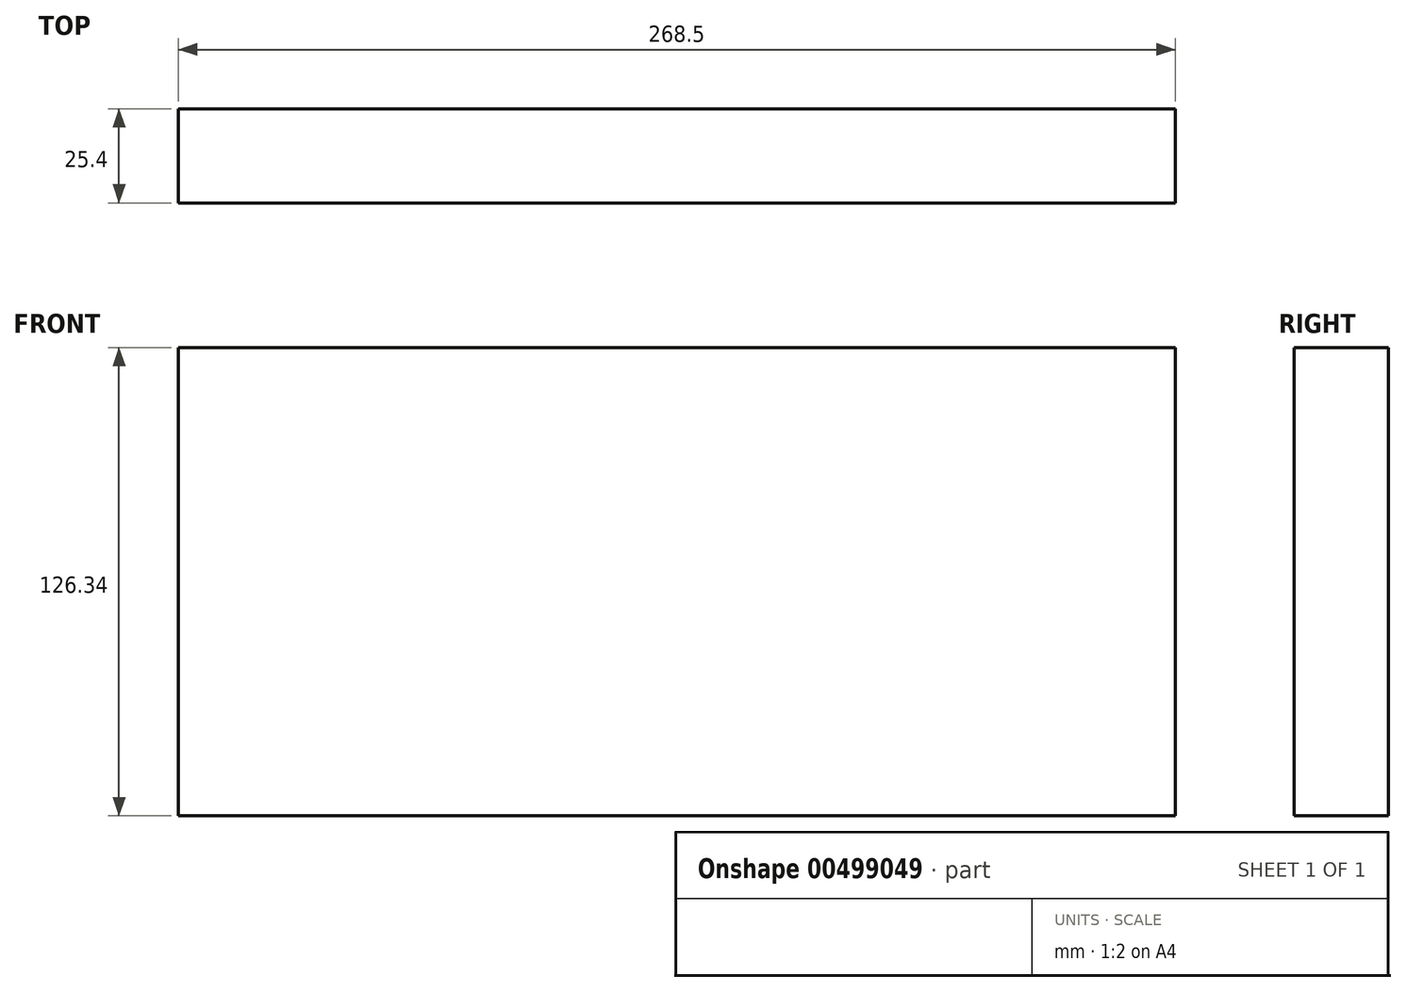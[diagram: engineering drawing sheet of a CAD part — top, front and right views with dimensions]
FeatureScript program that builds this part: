
annotation { "Feature Type Name" : "Feature", "Feature Type Description" : "" }
export const myFeature = defineFeature(function(context is Context, id is Id, definition is map)
    precondition{}
    {
        {
            var Q0;
            Q0=qCreatedBy(makeId("Front.planeOp"),FACE);
            var sketch = newSketch(context, id + "F0", { "sketchPlane" : qUnion([Q0])});
            skLineSegment(sketch, "E0.bottom", {"start": v(-133.99, 61.16) * mm, "end": v(134.5, 61.16) * mm});
            skLineSegment(sketch, "E0.top", {"start": v(-133.99, -65.18) * mm, "end": v(134.5, -65.18) * mm});
            skLineSegment(sketch, "E0.left", {"start": v(-133.99, 61.16) * mm, "end": v(-133.99, -65.18) * mm});
            skLineSegment(sketch, "E0.right", {"start": v(134.5, 61.16) * mm, "end": v(134.5, -65.18) * mm});
            skSolve(sketch);
        }
        {
            var Q0;
            Q0 = qSketchRegion(id + "F0", true);
            extrude(context, id + "F1", {"entities" : qUnion([Q0]), "depth" : 25.4 * mm});
        }
    });
